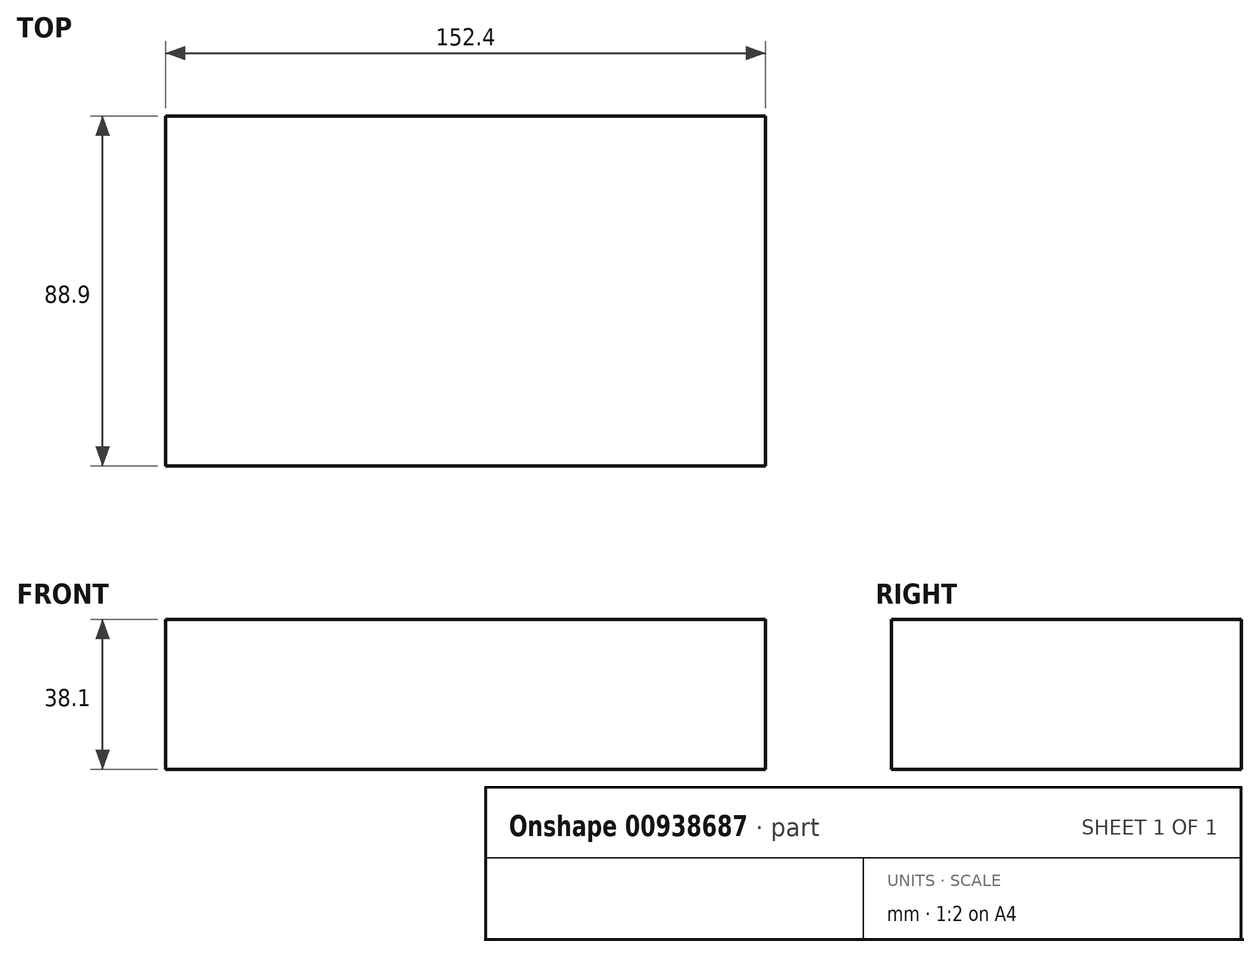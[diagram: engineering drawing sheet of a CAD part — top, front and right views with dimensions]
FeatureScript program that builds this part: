
annotation { "Feature Type Name" : "Feature", "Feature Type Description" : "" }
export const myFeature = defineFeature(function(context is Context, id is Id, definition is map)
    precondition{}
    {
        {
            var Q0;
            Q0=qCreatedBy(makeId("Right.planeOp"),FACE);
            var sketch = newSketch(context, id + "F0", { "sketchPlane" : qUnion([Q0])});
            skLineSegment(sketch, "E0.bottom", {"start": v(44.45, -19.05) * mm, "end": v(-44.45, -19.05) * mm});
            skLineSegment(sketch, "E0.top", {"start": v(44.45, 19.05) * mm, "end": v(-44.45, 19.05) * mm});
            skLineSegment(sketch, "E0.left", {"start": v(44.45, -19.05) * mm, "end": v(44.45, 19.05) * mm});
            skLineSegment(sketch, "E0.right", {"start": v(-44.45, -19.05) * mm, "end": v(-44.45, 19.05) * mm});
            skPoint(sketch, "E0.middle", {"position": v(0, 0) * mm});
            skSolve(sketch);
        }
        {
            var Q0;
            Q0=qSketchRegion(id+"F0",true);
            var Q1;
            Q1=makeQuery(id+"F0.imprint","IMPRINT",FACE,{"disambiguationData":[TD([[makeQuery(id+"F0.imprint","IMPRINT",EDGE,{"derivedFrom":sQuery(id+"F0.wireOp",EDGE,"E0.bottom")}),-1.0]])]});
            extrude(context, id + "F1", {"entities" : qUnion([Q0, Q1]), "depth" : 152.4 * mm, "offsetDistance" : 25.4 * mm});
        }
    });
